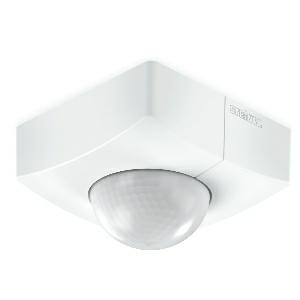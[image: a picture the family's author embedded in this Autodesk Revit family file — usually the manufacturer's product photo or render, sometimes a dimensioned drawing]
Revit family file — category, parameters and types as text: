
# Revit family: is_345_mx_highbay_057398
name_source: partatom
category: Elektroinstallationen
revit_build: Autodesk Revit 2016 (Build: 20190508_0715(x64)
units: mm (PartAtom-declared; Revit-internal decimal feet)

## family parameters
Basisbauteil = Fläche
Beim Laden mit Abzugskörper schneiden = Nein
Bemaßung runder Anschluss = Durchmesser verwenden
Beschriftungsausrichtung beibehalten = Nein
Gemeinsam genutzt = Nein
Raumberechnungspunkt = Nein
Teiletyp = Normal

## types (1)
- IS 345 MX Highbay
    Apparent Load = 0 VA
    Beschreibung = Type: Motion detectors; Dimensions (L x W x H): 65 x 95 x 95 mm; Mains power supply: 12 – 22,5 V / 50 – 60 Hz; Sensor Technology: passive infrared; Application, place: Indoors; Application, room: high-bay warehouse, Indoors; Installation site: ceiling; Installation: Surface wiring; Switching zones: 280 switching zones; Electronic scalability: No; Mechanical scalability: No; Mounting height: 4 – 14 m; Optimum mounting height: 12 m; Detection angle: 360 °; Angle of aperture: 45 °; Sneak-by guard: Yes; Capability of masking out individual segments: Yes; Reach, radial: 30 x 4 m (120 m²); Reach, tangential: 30 x 4 m (120 m²); Twilight setting TEACH: Yes; Twilight setting: 2 – 1000 lx; Time setting: 1 sec – 60 min; Control output, Dali: Addressable/slave; Constant-lighting control: No; Basic light level function: No; Basic light level function time: 1-30 min, all night; With bus coupling: Yes; Settings via: Bus; With remote control: No; Interconnection: Yes; IP-rating: IP54; Material: Plastic; Ambient temperature: -20 – 50 °C; Colour: white; Colour, RAL: 9003; Manufacturer's Warranty: 5 years; Version: DALI-2 IPD - surface, sq.; PU1, EAN: 4007841057398
    Height = 95 mm
    Hersteller = Steinel
    Length = 65 mm
    Maximum range = 3.441 m
    ModVariant = Nein
    Modell = 057398
    Mounting Place = Ceiling
    Mounting Type = Surface mounted
    Number of Poles = 1
    OnlyDefault = Ja
    Power Factor = 1
    Product Name = IS 345 MX Highbay
    Product group = Sensor-switched outdoor light
    ProductGroupID = 3
    Protection Class = Protection class
    Protection Degree = IP 54
    RlxData = <blob elided: 195197 chars, md5=e0f22c58>
    Sensor characteristics = Circular 300°-360°
    Sensor type = Passive (infrared)
    SensorDataFile = <blob elided: 170895 chars, md5=da062800>
    Type of entry = Motion
    Typenbild = produkt1_057398.jpg
    Typenkommentare = Product without accessories
    URL = http://relux.com
    VarID = ---
    Voltage = 0 V
    Vorgabe-Ansicht = 1800 mm
    Weight = 0.00 kg
    Width = 95 mm

## geometry (parser evidence)
native form markers: Sweep x16
no freeform markers — native parametric forms only
